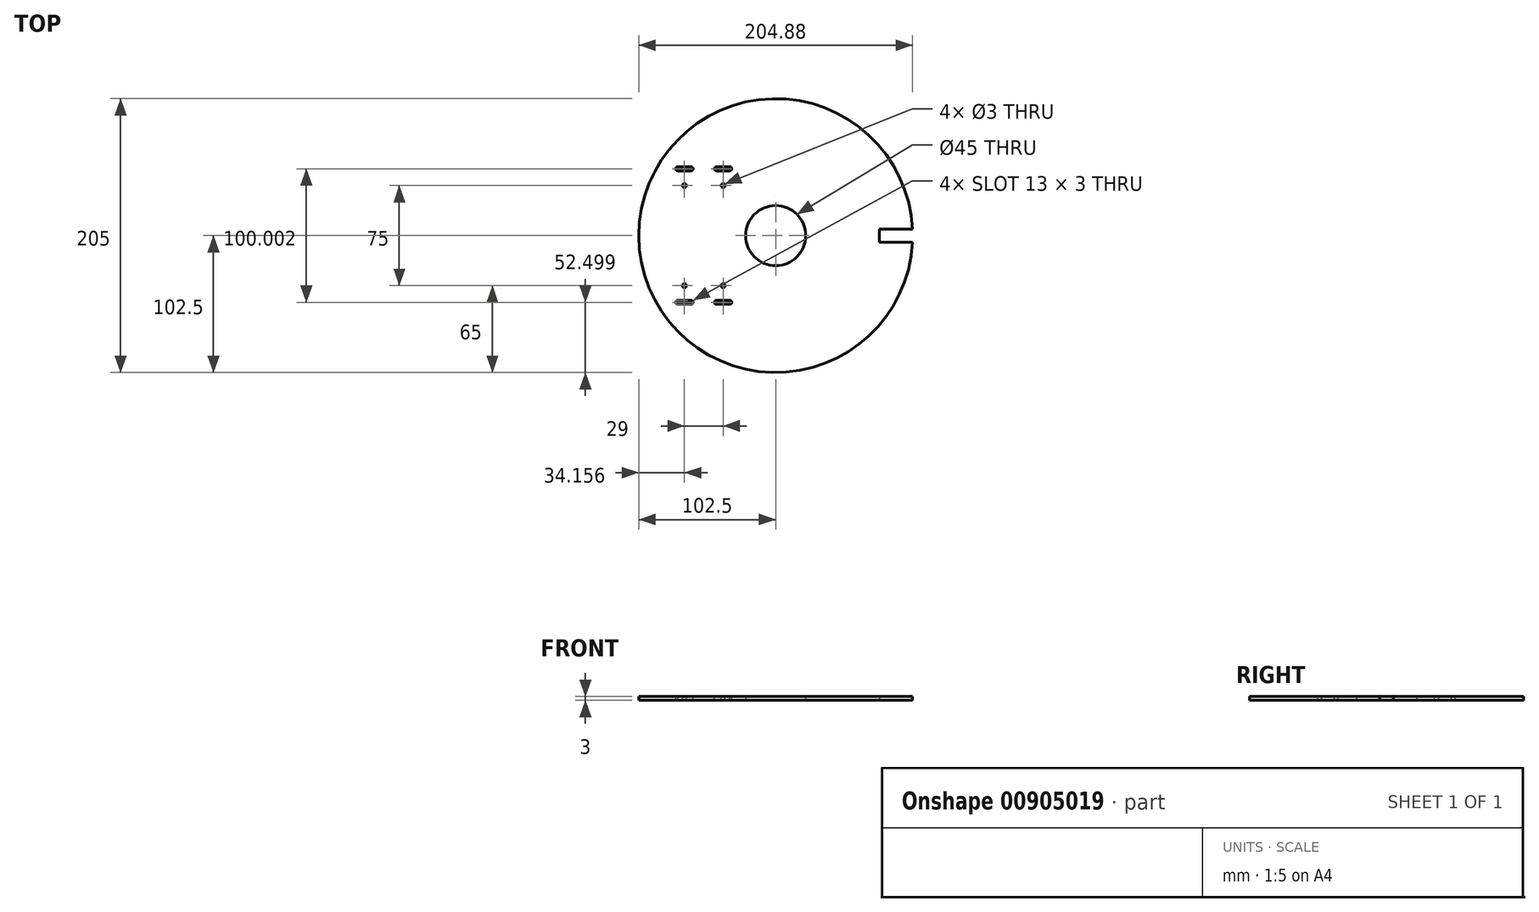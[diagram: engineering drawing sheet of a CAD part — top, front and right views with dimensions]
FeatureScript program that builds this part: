
annotation { "Feature Type Name" : "Feature", "Feature Type Description" : "" }
export const myFeature = defineFeature(function(context is Context, id is Id, definition is map)
    precondition{}
    {
        {
            var Q0;
            Q0=qCreatedBy(makeId("Top.planeOp"),FACE);
            var sketch = newSketch(context, id + "F0", { "sketchPlane" : qUnion([Q0])});
            skArc(sketch, "E0", {"start": v(102.38, 5) * mm, "mid": v(-102.5, 0) * mm, "end": v(102.38, -5) * mm});
            skLineSegment(sketch, "E1", {"start": v(-152.5, 0) * mm, "end": v(164.42, 0) * mm, "construction": true});
            skLineSegment(sketch, "E2", {"start": v(0, 131.27) * mm, "end": v(0, -153.08) * mm, "construction": true});
            skLineSegment(sketch, "E3.bottom", {"start": v(102.38, -5) * mm, "end": v(77.5, -5) * mm});
            skLineSegment(sketch, "E3.top", {"start": v(102.38, 5) * mm, "end": v(77.5, 5) * mm});
            skLineSegment(sketch, "E3.right", {"start": v(77.5, -5) * mm, "end": v(77.5, 5) * mm});
            skCircle(sketch, "E4", {"center": v(0, 0) * mm, "radius": 22.5 * mm});
            skSolve(sketch);
        }
        {
            var Q0;
            Q0=makeQuery(id+"F0.imprint","IMPRINT",FACE,{"disambiguationData":[TD([[makeQuery(id+"F0.imprint","IMPRINT",EDGE,{"derivedFrom":sQuery(id+"F0.wireOp",EDGE,"E0")}),1.0]])]});
            extrude(context, id + "F1", {"entities" : qUnion([Q0]), "depth" : 3 * mm, "offsetDistance" : 25 * mm});
        }
        {
            var Q0;
            Q0=makeQuery(id+"F1.opExtrude","CAP_FACE",FACE,{"disambiguationData":[OSD([sQuery(id+"F0.wireOp",EDGE,"E0"),sQuery(id+"F0.wireOp",EDGE,"E3.bottom"),sQuery(id+"F0.wireOp",EDGE,"E3.top"),sQuery(id+"F0.wireOp",EDGE,"E3.right"),sQuery(id+"F0.wireOp",EDGE,"E4")])],"isStart":false});
            var sketch = newSketch(context, id + "F2", { "sketchPlane" : qUnion([Q0])});
            skLineSegment(sketch, "E5.bottom", {"start": v(-34.34, -43.5) * mm, "end": v(-73.34, -43.5) * mm, "construction": true});
            skLineSegment(sketch, "E5.top", {"start": v(-34.34, 43.5) * mm, "end": v(-73.34, 43.5) * mm, "construction": true});
            skLineSegment(sketch, "E5.left", {"start": v(-34.34, -43.5) * mm, "end": v(-34.34, 43.5) * mm, "construction": true});
            skLineSegment(sketch, "E5.right", {"start": v(-73.34, -43.5) * mm, "end": v(-73.34, 43.5) * mm, "construction": true});
            skPoint(sketch, "E5.middle", {"position": v(-53.84, 0) * mm});
            skLineSegment(sketch, "E6", {"start": v(-68.34, 43.5) * mm, "end": v(-68.34, -43.5) * mm, "construction": true});
            skLineSegment(sketch, "E7", {"start": v(-73.34, 37.5) * mm, "end": v(-34.34, 37.5) * mm, "construction": true});
            skCircle(sketch, "E8", {"center": v(-68.34, 37.5) * mm, "radius": 1.5 * mm});
            skLineSegment(sketch, "E9", {"start": v(-53.84, 51.85) * mm, "end": v(-53.84, -62.72) * mm, "construction": true});
            skCircle(sketch, "E10.MirrorC", {"center": v(-39.34, 37.5) * mm, "radius": 1.5 * mm});
            skLineSegment(sketch, "E11", {"start": v(-78.66, 0) * mm, "end": v(-24.75, 0) * mm, "construction": true});
            skCircle(sketch, "E12.MirrorC", {"center": v(-39.34, -37.5) * mm, "radius": 1.5 * mm});
            skCircle(sketch, "E13.MirrorC", {"center": v(-68.34, -37.5) * mm, "radius": 1.5 * mm});
            skArc(sketch, "E14", {"start": v(-73.25, 51.5) * mm, "mid": v(-74.84, 50.02) * mm, "end": v(-73.3, 48.5) * mm});
            skArc(sketch, "E15.MirrorC", {"start": v(-63.34, 51.5) * mm, "mid": v(-61.84, 50) * mm, "end": v(-63.34, 48.5) * mm});
            skLineSegment(sketch, "E16", {"start": v(-73.44, 51.5) * mm, "end": v(-63.34, 51.5) * mm});
            skLineSegment(sketch, "E17", {"start": v(-73.4, 48.5) * mm, "end": v(-63.34, 48.5) * mm});
            skLineSegment(sketch, "E18.MirrorCS", {"start": v(-34.25, 51.5) * mm, "end": v(-44.34, 51.5) * mm});
            skArc(sketch, "E19.MirrorCS", {"start": v(-34.44, 51.5) * mm, "mid": v(-32.84, 50.02) * mm, "end": v(-34.4, 48.5) * mm});
            skLineSegment(sketch, "E20.MirrorCS", {"start": v(-34.3, 48.5) * mm, "end": v(-44.34, 48.5) * mm});
            skArc(sketch, "E21.MirrorCS", {"start": v(-44.34, 51.5) * mm, "mid": v(-45.84, 50) * mm, "end": v(-44.34, 48.5) * mm});
            skLineSegment(sketch, "E22.MirrorCS", {"start": v(-34.25, -51.5) * mm, "end": v(-44.34, -51.5) * mm});
            skLineSegment(sketch, "E23.MirrorCS", {"start": v(-34.3, -48.5) * mm, "end": v(-44.34, -48.5) * mm});
            skArc(sketch, "E24.MirrorCS", {"start": v(-34.44, -51.5) * mm, "mid": v(-32.84, -50.02) * mm, "end": v(-34.4, -48.5) * mm});
            skArc(sketch, "E25.MirrorCS", {"start": v(-44.34, -51.5) * mm, "mid": v(-45.84, -50) * mm, "end": v(-44.34, -48.5) * mm});
            skArc(sketch, "E26.MirrorCS", {"start": v(-73.25, -51.5) * mm, "mid": v(-74.84, -50.02) * mm, "end": v(-73.3, -48.5) * mm});
            skLineSegment(sketch, "E27.MirrorCS", {"start": v(-73.44, -51.5) * mm, "end": v(-63.34, -51.5) * mm});
            skLineSegment(sketch, "E28.MirrorCS", {"start": v(-73.4, -48.5) * mm, "end": v(-63.34, -48.5) * mm});
            skArc(sketch, "E29.MirrorCS", {"start": v(-63.34, -51.5) * mm, "mid": v(-61.84, -50) * mm, "end": v(-63.34, -48.5) * mm});
            skSolve(sketch);
        }
        {
            var Q0;
            Q0 = qSketchRegion(id + "F2", true);
            extrude(context, id + "F3", {"entities" : qUnion([Q0]), "operationType" : NewBodyOperationType.REMOVE, "oppositeDirection" : true, "depth" : 25 * mm, "offsetDistance" : 25 * mm});
        }
    });
